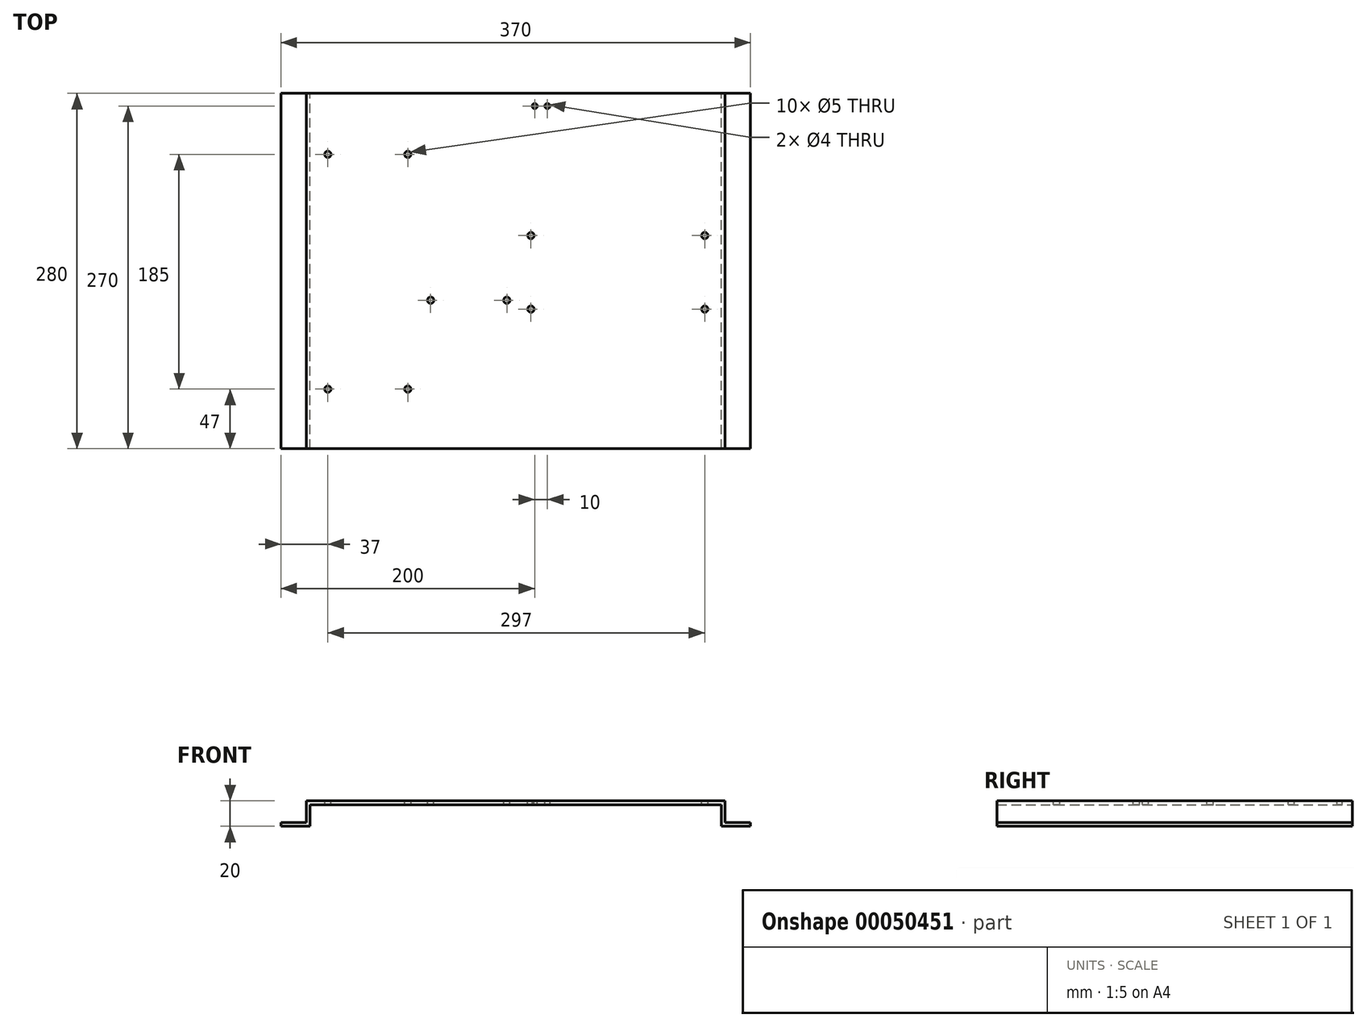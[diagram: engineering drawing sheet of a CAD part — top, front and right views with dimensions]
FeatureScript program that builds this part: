
annotation { "Feature Type Name" : "Feature", "Feature Type Description" : "" }
export const myFeature = defineFeature(function(context is Context, id is Id, definition is map)
    precondition{}
    {
        {
            var Q0;
            Q0=qCreatedBy(makeId("Front.planeOp"),FACE);
            var sketch = newSketch(context, id + "F0", { "sketchPlane" : qUnion([Q0])});
            skLineSegment(sketch, "E0", {"start": v(-162, 0) * mm, "end": v(162, 0) * mm});
            skLineSegment(sketch, "E1.0", {"start": v(-165, 3) * mm, "end": v(165, 3) * mm});
            skLineSegment(sketch, "E2", {"start": v(-165, 3) * mm, "end": v(-165, -14) * mm});
            skLineSegment(sketch, "E3", {"start": v(165, 3) * mm, "end": v(165, -14) * mm});
            skLineSegment(sketch, "E4", {"start": v(165, -14) * mm, "end": v(185, -14) * mm});
            skLineSegment(sketch, "E5", {"start": v(-165, -14) * mm, "end": v(-185, -14) * mm});
            skLineSegment(sketch, "E6", {"start": v(-162, 0) * mm, "end": v(-162, -17) * mm});
            skLineSegment(sketch, "E7", {"start": v(162, 0) * mm, "end": v(162, -17) * mm});
            skLineSegment(sketch, "E8", {"start": v(-185, -14) * mm, "end": v(-185, -17) * mm});
            skLineSegment(sketch, "E9", {"start": v(-185, -17) * mm, "end": v(-162, -17) * mm});
            skLineSegment(sketch, "E10", {"start": v(185, -14) * mm, "end": v(185, -17) * mm});
            skLineSegment(sketch, "E11", {"start": v(185, -17) * mm, "end": v(162, -17) * mm});
            skSolve(sketch);
        }
        {
            var Q0;
            Q0 = qSketchRegion(id + "F0", true);
            extrude(context, id + "F1", {"entities" : qUnion([Q0]), "depth" : 280 * mm});
        }
        {
            var Q0;
            Q0=makeQuery(id+"F1.opExtrude","SWEPT_FACE",FACE,{"disambiguationData":[OSD([sQuery(id+"F0.wireOp",EDGE,"E1.0")])]});
            var sketch = newSketch(context, id + "F2", { "sketchPlane" : qUnion([Q0])});
            skPoint(sketch, "E12.centerSnap0", {"position": v(0, -140) * mm});
            skCircle(sketch, "E13", {"center": v(-148, -48) * mm, "radius": 2.5 * mm});
            skCircle(sketch, "E14", {"center": v(15, -10) * mm, "radius": 2 * mm});
            skCircle(sketch, "E15", {"center": v(25, -10) * mm, "radius": 2 * mm});
            skCircle(sketch, "E16.MirrorC", {"center": v(-85, -48) * mm, "radius": 2.5 * mm});
            skCircle(sketch, "E17.MirrorC", {"center": v(-85, -233) * mm, "radius": 2.5 * mm});
            skCircle(sketch, "E18.MirrorC", {"center": v(-148, -233) * mm, "radius": 2.5 * mm});
            skCircle(sketch, "E19", {"center": v(149, -112) * mm, "radius": 2.5 * mm});
            skCircle(sketch, "E20.MirrorC", {"center": v(12, -112) * mm, "radius": 2.5 * mm});
            skCircle(sketch, "E21.MirrorC", {"center": v(12, -170) * mm, "radius": 2.5 * mm});
            skCircle(sketch, "E22.MirrorC", {"center": v(149, -170) * mm, "radius": 2.5 * mm});
            skCircle(sketch, "E23", {"center": v(-67, -163) * mm, "radius": 2.5 * mm});
            skCircle(sketch, "E24", {"center": v(-7, -163) * mm, "radius": 2.5 * mm});
            skSolve(sketch);
        }
        {
            var Q0;
            Q0 = qSketchRegion(id + "F2", true);
            extrude(context, id + "F3", {"entities" : qUnion([Q0]), "operationType" : NewBodyOperationType.REMOVE, "oppositeDirection" : true, "depth" : 25 * mm});
        }
    });
